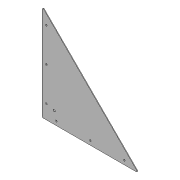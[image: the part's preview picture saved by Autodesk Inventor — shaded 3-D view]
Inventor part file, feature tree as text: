
AUTODESK INVENTOR PART (.ipt)
format: ipt  version: 2020 (Build 240168000, 168)  size: 168,448 bytes
history: native  units: mm
features: sketch x6, hole x4, projected_geometry x3, other x2, fillet x1, extrude x1
ambient origin geometry x8: Origin, YZ Plane, XZ Plane, XY Plane, X Axis, Y Axis, Z Axis, Center Point
bodies: Body1 (feature_tree)
feature tree (17):
  other  "ソリッド1"
  hole  "穴1"  [1 undecoded]
  fillet  "フィレット1"  Radius=20.0mm
  hole  "穴2"  [1 undecoded]
  hole  "穴3"  [1 undecoded]
  hole  "穴4"  [1 undecoded]
  extrude  "押し出し2"  Depth=20.594885mm
  sketch  "スケッチ1"
  other  "プレート1"
  sketch  "スケッチ2"
  sketch  "スケッチ3"
  sketch  "スケッチ4"
  projected_geometry  "投影ループ1"
  sketch  "スケッチ6"
  projected_geometry  "投影ループ3"
  sketch  "スケッチ7"
  projected_geometry  "投影ループ4"
note: 4 required parameter values undecoded (feature->parameter linkage not recoverable at this tier; creation-order binding heuristic only, values carry confidence <= 0.55)
